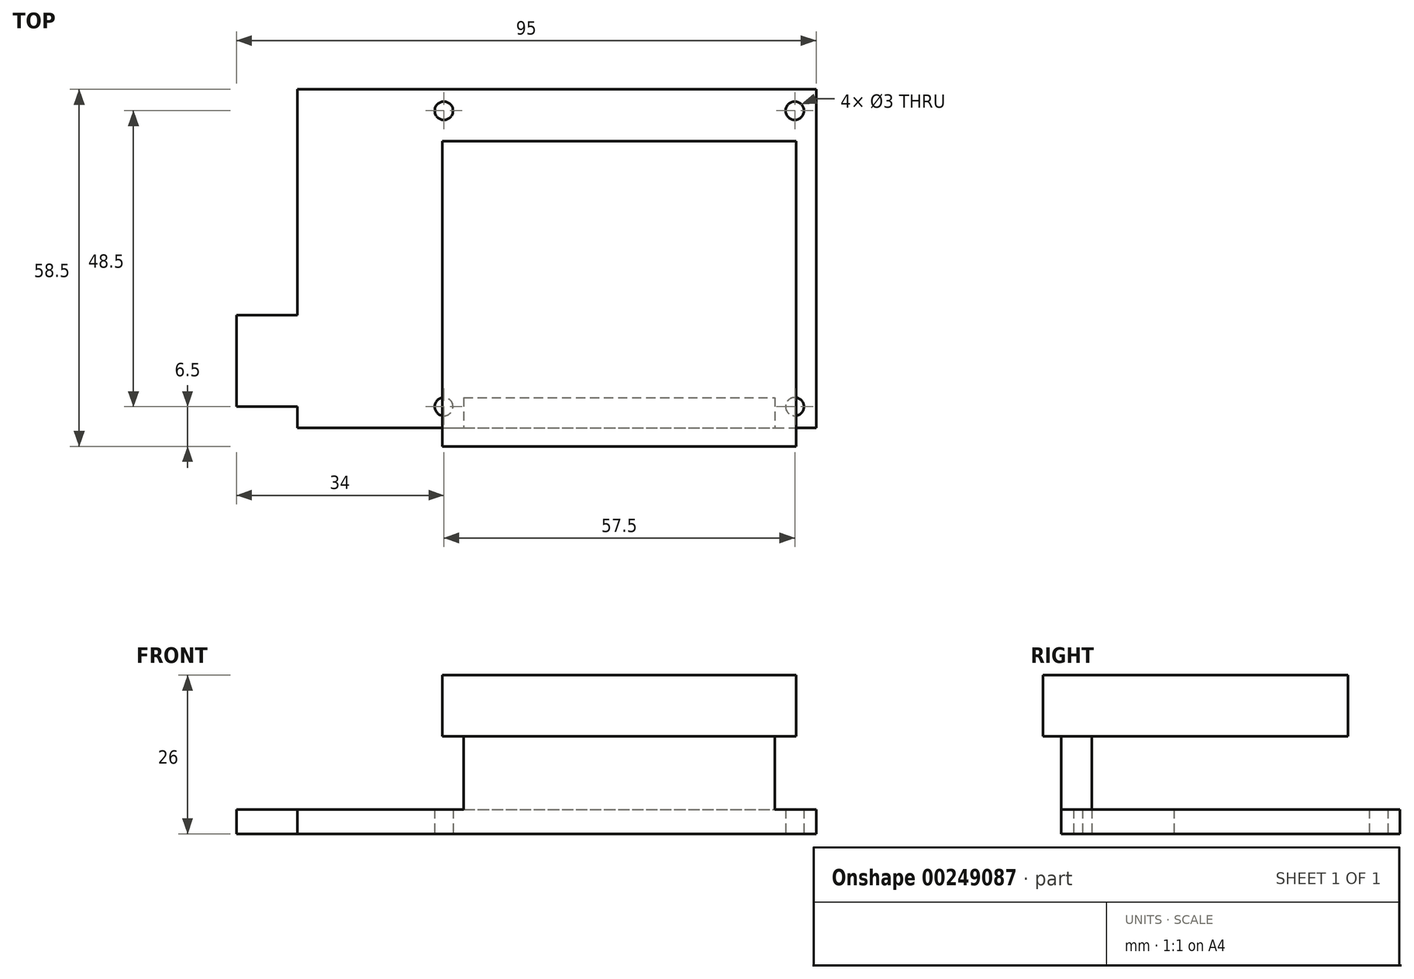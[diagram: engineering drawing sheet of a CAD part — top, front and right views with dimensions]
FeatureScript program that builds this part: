
annotation { "Feature Type Name" : "Feature", "Feature Type Description" : "" }
export const myFeature = defineFeature(function(context is Context, id is Id, definition is map)
    precondition{}
    {
        {
            var Q0;
            Q0=qCreatedBy(makeId("Top.planeOp"),FACE);
            var sketch = newSketch(context, id + "F0", { "sketchPlane" : qUnion([Q0])});
            skLineSegment(sketch, "E0.bottom", {"start": v(-42.5, 27.75) * mm, "end": v(42.5, 27.75) * mm});
            skLineSegment(sketch, "E0.top", {"start": v(-42.5, -27.75) * mm, "end": v(42.5, -27.75) * mm});
            skLineSegment(sketch, "E0.left", {"start": v(-42.5, 27.75) * mm, "end": v(-42.5, -27.75) * mm});
            skLineSegment(sketch, "E0.right", {"start": v(42.5, 27.75) * mm, "end": v(42.5, -27.75) * mm});
            skCircle(sketch, "E1", {"center": v(39, 24.25) * mm, "radius": 1.5 * mm});
            skPoint(sketch, "E2", {"position": v(0, 27.75) * mm});
            skPoint(sketch, "E3", {"position": v(-42.5, 0) * mm});
            skCircle(sketch, "E4", {"center": v(-18.5, 24.25) * mm, "radius": 1.5 * mm});
            skCircle(sketch, "E5.MirrorC", {"center": v(-18.5, -24.25) * mm, "radius": 1.5 * mm});
            skCircle(sketch, "E6.MirrorC", {"center": v(39, -24.25) * mm, "radius": 1.5 * mm});
            skLineSegment(sketch, "E7.bottom", {"start": v(-42.5, -24.25) * mm, "end": v(-52.5, -24.25) * mm});
            skLineSegment(sketch, "E7.top", {"start": v(-42.5, -9.25) * mm, "end": v(-52.5, -9.25) * mm});
            skLineSegment(sketch, "E7.left", {"start": v(-42.5, -24.25) * mm, "end": v(-42.5, -9.25) * mm});
            skLineSegment(sketch, "E7.right", {"start": v(-52.5, -24.25) * mm, "end": v(-52.5, -9.25) * mm});
            skSolve(sketch);
        }
        {
            var Q0;
            Q0 = qSketchRegion(id + "F0", true);
            extrude(context, id + "F1", {"entities" : qUnion([Q0]), "depth" : 4 * mm});
        }
        {
            var Q0;
            Q0=makeQuery(id+"F1.opExtrude","CAP_FACE",FACE,{"disambiguationData":[OSD([sQuery(id+"F0.wireOp",EDGE,"E0.bottom"),sQuery(id+"F0.wireOp",EDGE,"E0.top"),sQuery(id+"F0.wireOp",EDGE,"E0.left"),sQuery(id+"F0.wireOp",EDGE,"E0.right"),sQuery(id+"F0.wireOp",EDGE,"E1"),sQuery(id+"F0.wireOp",EDGE,"E4"),sQuery(id+"F0.wireOp",EDGE,"E5.MirrorC"),sQuery(id+"F0.wireOp",EDGE,"E6.MirrorC"),sQuery(id+"F0.wireOp",EDGE,"E7.bottom"),sQuery(id+"F0.wireOp",EDGE,"E7.top"),sQuery(id+"F0.wireOp",EDGE,"E7.right")])],"isStart":false});
            var sketch = newSketch(context, id + "F2", { "sketchPlane" : qUnion([Q0])});
            skLineSegment(sketch, "E8.bottom", {"start": v(-15.25, -22.75) * mm, "end": v(35.75, -22.75) * mm});
            skLineSegment(sketch, "E8.top", {"start": v(-15.25, -27.75) * mm, "end": v(35.75, -27.75) * mm});
            skLineSegment(sketch, "E8.left", {"start": v(-15.25, -22.75) * mm, "end": v(-15.25, -27.75) * mm});
            skLineSegment(sketch, "E8.right", {"start": v(35.75, -22.75) * mm, "end": v(35.75, -27.75) * mm});
            skPoint(sketch, "E9", {"position": v(10.25, -22.75) * mm});
            skLineSegment(sketch, "E10", {"start": v(-18.5, -24.25) * mm, "end": v(39, -24.25) * mm, "construction": true});
            skPoint(sketch, "E11", {"position": v(10.25, -24.25) * mm});
            skSolve(sketch);
        }
        {
            var Q0;
            Q0 = qSketchRegion(id + "F2", true);
            extrude(context, id + "F3", {"entities" : qUnion([Q0]), "operationType" : NewBodyOperationType.ADD, "depth" : 12 * mm});
        }
        {
            var Q0;
            Q0=makeQuery(id+"F3.opExtrude","CAP_FACE",FACE,{"disambiguationData":[OSD([sQuery(id+"F2.wireOp",EDGE,"E8.bottom"),sQuery(id+"F2.wireOp",EDGE,"E8.top"),sQuery(id+"F2.wireOp",EDGE,"E8.left"),sQuery(id+"F2.wireOp",EDGE,"E8.right")])],"isStart":false});
            var sketch = newSketch(context, id + "F4", { "sketchPlane" : qUnion([Q0])});
            skLineSegment(sketch, "E12.bottom", {"start": v(-18.75, 19.25) * mm, "end": v(39.25, 19.25) * mm});
            skLineSegment(sketch, "E12.top", {"start": v(-18.75, -30.75) * mm, "end": v(39.25, -30.75) * mm});
            skLineSegment(sketch, "E12.left", {"start": v(-18.75, 19.25) * mm, "end": v(-18.75, -30.75) * mm});
            skLineSegment(sketch, "E12.right", {"start": v(39.25, 19.25) * mm, "end": v(39.25, -30.75) * mm});
            skPoint(sketch, "E13", {"position": v(10.25, -30.75) * mm});
            skPoint(sketch, "E14", {"position": v(10.25, -27.75) * mm});
            skSolve(sketch);
        }
        {
            var Q0;
            Q0 = qSketchRegion(id + "F4", true);
            extrude(context, id + "F5", {"entities" : qUnion([Q0]), "operationType" : NewBodyOperationType.ADD, "depth" : 10 * mm});
        }
    });
